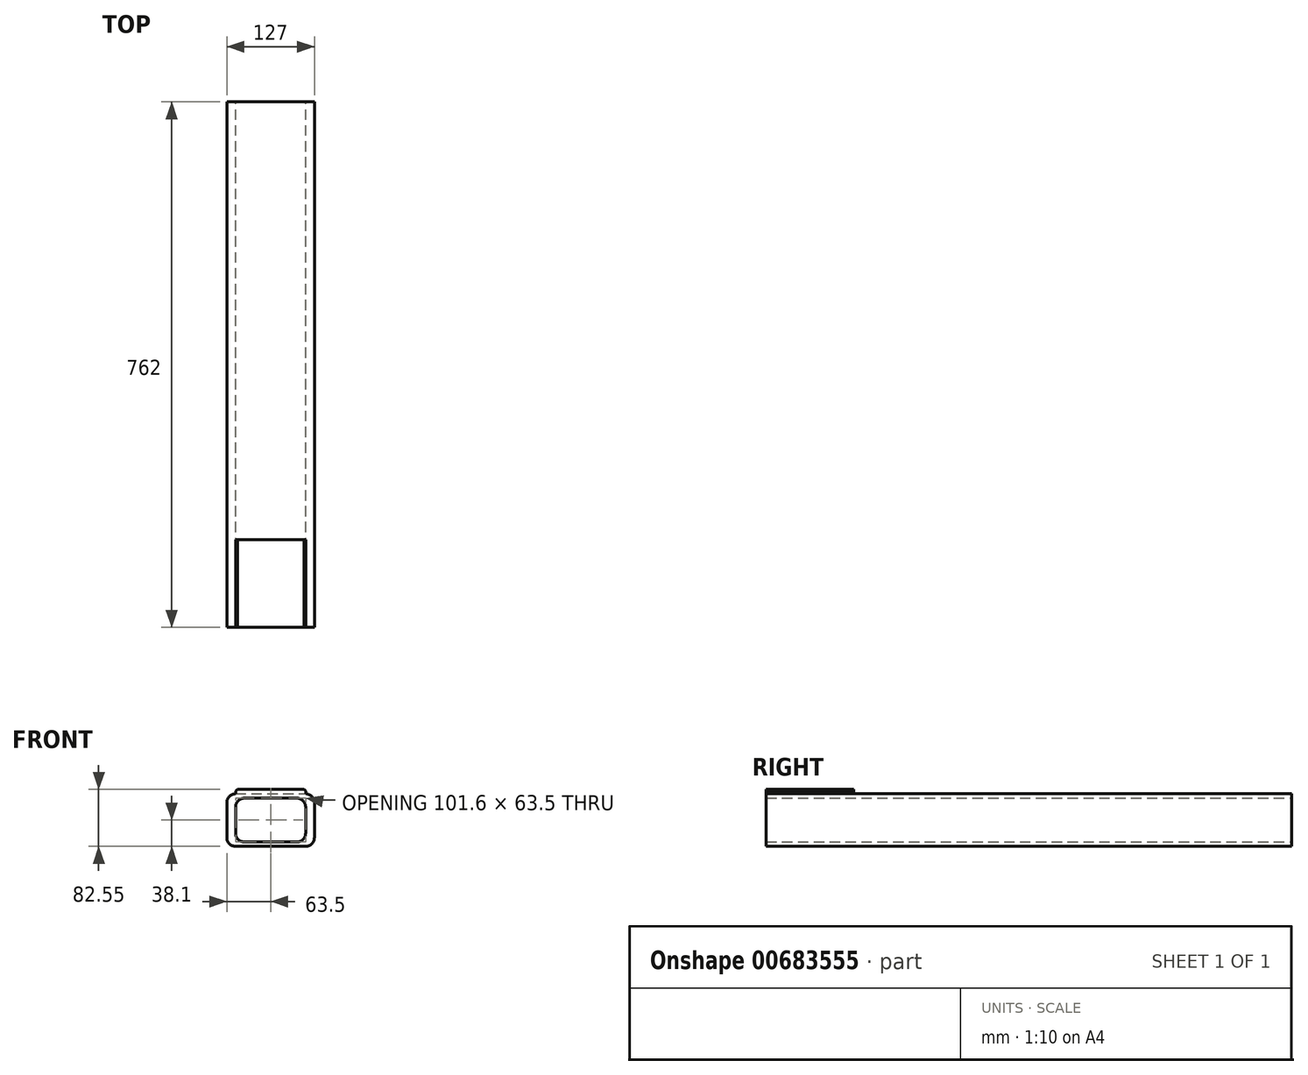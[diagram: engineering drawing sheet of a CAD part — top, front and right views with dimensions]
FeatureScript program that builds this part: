
annotation { "Feature Type Name" : "Feature", "Feature Type Description" : "" }
export const myFeature = defineFeature(function(context is Context, id is Id, definition is map)
    precondition{}
    {
        {
            var Q0;
            Q0=qCreatedBy(makeId("Front.planeOp"),FACE);
            var sketch = newSketch(context, id + "F0", { "sketchPlane" : qUnion([Q0])});
            skLineSegment(sketch, "E0.bottom", {"start": v(38.1, 31.75) * mm, "end": v(-38.1, 31.75) * mm});
            skLineSegment(sketch, "E0.top", {"start": v(38.1, -31.75) * mm, "end": v(-38.1, -31.75) * mm});
            skLineSegment(sketch, "E0.left", {"start": v(50.8, 19.05) * mm, "end": v(50.8, -19.05) * mm});
            skLineSegment(sketch, "E0.right", {"start": v(-50.8, 19.05) * mm, "end": v(-50.8, -19.05) * mm});
            skPoint(sketch, "E0.middle", {"position": v(0, 0) * mm});
            skPoint(sketch, "E1.visualSharp", {"position": v(-50.8, 31.75) * mm});
            skArc(sketch, "E1.filletArc", {"start": v(-38.1, 31.75) * mm, "mid": v(-47.08, 28.03) * mm, "end": v(-50.8, 19.05) * mm});
            skPoint(sketch, "E2.visualSharp", {"position": v(50.8, 31.75) * mm});
            skArc(sketch, "E2.filletArc", {"start": v(50.8, 19.05) * mm, "mid": v(47.08, 28.03) * mm, "end": v(38.1, 31.75) * mm});
            skPoint(sketch, "E3.visualSharp", {"position": v(50.8, -31.75) * mm});
            skArc(sketch, "E3.filletArc", {"start": v(38.1, -31.75) * mm, "mid": v(47.08, -28.03) * mm, "end": v(50.8, -19.05) * mm});
            skPoint(sketch, "E4.visualSharp", {"position": v(-50.8, -31.75) * mm});
            skArc(sketch, "E4.filletArc", {"start": v(-50.8, -19.05) * mm, "mid": v(-47.08, -28.03) * mm, "end": v(-38.1, -31.75) * mm});
            skLineSegment(sketch, "E5.bottom", {"start": v(50.8, 38.1) * mm, "end": v(-50.8, 38.1) * mm});
            skLineSegment(sketch, "E5.top", {"start": v(50.8, -38.1) * mm, "end": v(-50.8, -38.1) * mm});
            skLineSegment(sketch, "E5.left", {"start": v(63.5, 25.4) * mm, "end": v(63.5, -25.4) * mm});
            skLineSegment(sketch, "E5.right", {"start": v(-63.5, 25.4) * mm, "end": v(-63.5, -25.4) * mm});
            skPoint(sketch, "E6.visualSharp", {"position": v(-63.5, 38.1) * mm});
            skArc(sketch, "E6.filletArc", {"start": v(-50.8, 38.1) * mm, "mid": v(-59.78, 34.38) * mm, "end": v(-63.5, 25.4) * mm});
            skPoint(sketch, "E7.visualSharp", {"position": v(63.5, 38.1) * mm});
            skArc(sketch, "E7.filletArc", {"start": v(63.5, 25.4) * mm, "mid": v(59.78, 34.38) * mm, "end": v(50.8, 38.1) * mm});
            skPoint(sketch, "E8.visualSharp", {"position": v(63.5, -38.1) * mm});
            skArc(sketch, "E8.filletArc", {"start": v(50.8, -38.1) * mm, "mid": v(59.78, -34.38) * mm, "end": v(63.5, -25.4) * mm});
            skPoint(sketch, "E9.visualSharp", {"position": v(-63.5, -38.1) * mm});
            skArc(sketch, "E9.filletArc", {"start": v(-63.5, -25.4) * mm, "mid": v(-59.78, -34.38) * mm, "end": v(-50.8, -38.1) * mm});
            skSolve(sketch);
        }
        {
            var Q0;
            Q0=makeQuery(id+"F0.imprint","IMPRINT",FACE,{"disambiguationData":[TD([[makeQuery(id+"F0.imprint","IMPRINT",EDGE,{"derivedFrom":sQuery(id+"F0.wireOp",EDGE,"E0.bottom")}),-1.0]])]});
            extrude(context, id + "F1", {"entities" : qUnion([Q0]), "depth" : 762 * mm, "offsetDistance" : 25.4 * mm});
        }
        {
            var Q0;
            Q0=makeQuery(id+"F1.opExtrude","SWEPT_FACE",FACE,{"disambiguationData":[OSD([sQuery(id+"F0.wireOp",EDGE,"E5.bottom")])]});
            var sketch = newSketch(context, id + "F2", { "sketchPlane" : qUnion([Q0])});
            skLineSegment(sketch, "E10.bottom", {"start": v(-50.8, -762) * mm, "end": v(50.8, -762) * mm});
            skLineSegment(sketch, "E10.top", {"start": v(-50.8, -635) * mm, "end": v(50.8, -635) * mm});
            skLineSegment(sketch, "E10.left", {"start": v(-50.8, -762) * mm, "end": v(-50.8, -635) * mm});
            skLineSegment(sketch, "E10.right", {"start": v(50.8, -762) * mm, "end": v(50.8, -635) * mm});
            skSolve(sketch);
        }
        {
            var Q0;
            Q0 = qSketchRegion(id + "F2", true);
            extrude(context, id + "F3", {"entities" : qUnion([Q0]), "operationType" : NewBodyOperationType.ADD, "depth" : 6.35 * mm, "offsetDistance" : 25.4 * mm});
        }
        {
            var Q0;
            Q0=makeQuery(id+"F3.opExtrude","CAP_EDGE",EDGE,{"disambiguationData":[OSD([sQuery(id+"F2.wireOp",EDGE,"E10.right")])],"isStart":false});
            var Q1;
            Q1=makeQuery(id+"F3.opExtrude","CAP_EDGE",EDGE,{"disambiguationData":[OSD([sQuery(id+"F2.wireOp",EDGE,"E10.left")])],"isStart":false});
            chamfer(context, id + "F4", {"entities" : qUnion([Q0, Q1]), "width" : 2.54 * mm, "tangentPropagation" : true});
        }
    });
